# Revit family: BDG_BossDesign_Stng_PeekAndBoo
name_source: partatom
category: Furniture
revit_build: Autodesk Revit 2015 (Build: 20140903_1530(x64)
units: mm (PartAtom-declared; Revit-internal decimal feet)

## types (2) — shared parameters
Assembly Code = E2020200
AssetType = Movable
BIMObjectName = BDG_BossDesign_Seating_PeekAndBoo
Category = Pr_40_50_12 : Chairs, seats and benches
DurationUnit = year
ExpectedLife = 5
Finish = Fully upholstered with swivel
IfcExportAs = IfcFurnishingElementType
IfcExportType = CHAIR
Keynote = Pr_40_50_12
ManufacturerName = Boss Design
ManufacturerURL = www.bossdesign.com
Material = Fabric
NBSDescription = Seating
NBSReference = 45-35-72/352
Name = Seating_PeekAndBoo_BossDesign
ProductInformation = www.bossdesign.com/product-list/peek-boo
Shape = Circular
URL = www.bossdesign.com
Uniclass2015Code = Pr_40_50_12
Uniclass2015Title = Chairs, seats and benches
Uniclass2015Version = Products v1.10
Version = 1
WarrantyDescription = Structural Warranty Excludes Foams and Fabrics
WarrantyDurationLabor = 5
WarrantyDurationParts = 5
WarrantyDurationUnit = year

## per-type parameters (varying)
| type | Color | Description | IsScreen | MainColor | Model | ModelNumber | ModelReference | NominalHeight | NominalLength | NominalWidth | Size |
| Boo with Swivel | Blue | Boo with swivel | No | Blue | BOO/1 | BOO/1 | Boo with swivel | 755 mm  [stored 2.47703 ft] | 910 mm | 676 mm  [stored 2.21785 ft] | 910 x 676 x 755mm |
| Peek Upholstered Screen with Boo Unit | Blue and Grey | Peek upholstered screen with Boo unit | Yes | Blue and Grey | PEK/1 | PEK/1 | Peek upholstered screen with Boo unit | 1455 mm  [stored 4.77362 ft] | 725 mm  [stored 2.37861 ft] | 1006 mm  [stored 3.30052 ft] | 1006 x 725 x 1455mm |

note: [stored X ft] marks values corroborated as IEEE doubles in the binary element streams (Revit-internal decimal feet)

## geometry (parser evidence)
native form markers: Sweep x2
no freeform markers — native parametric forms only
